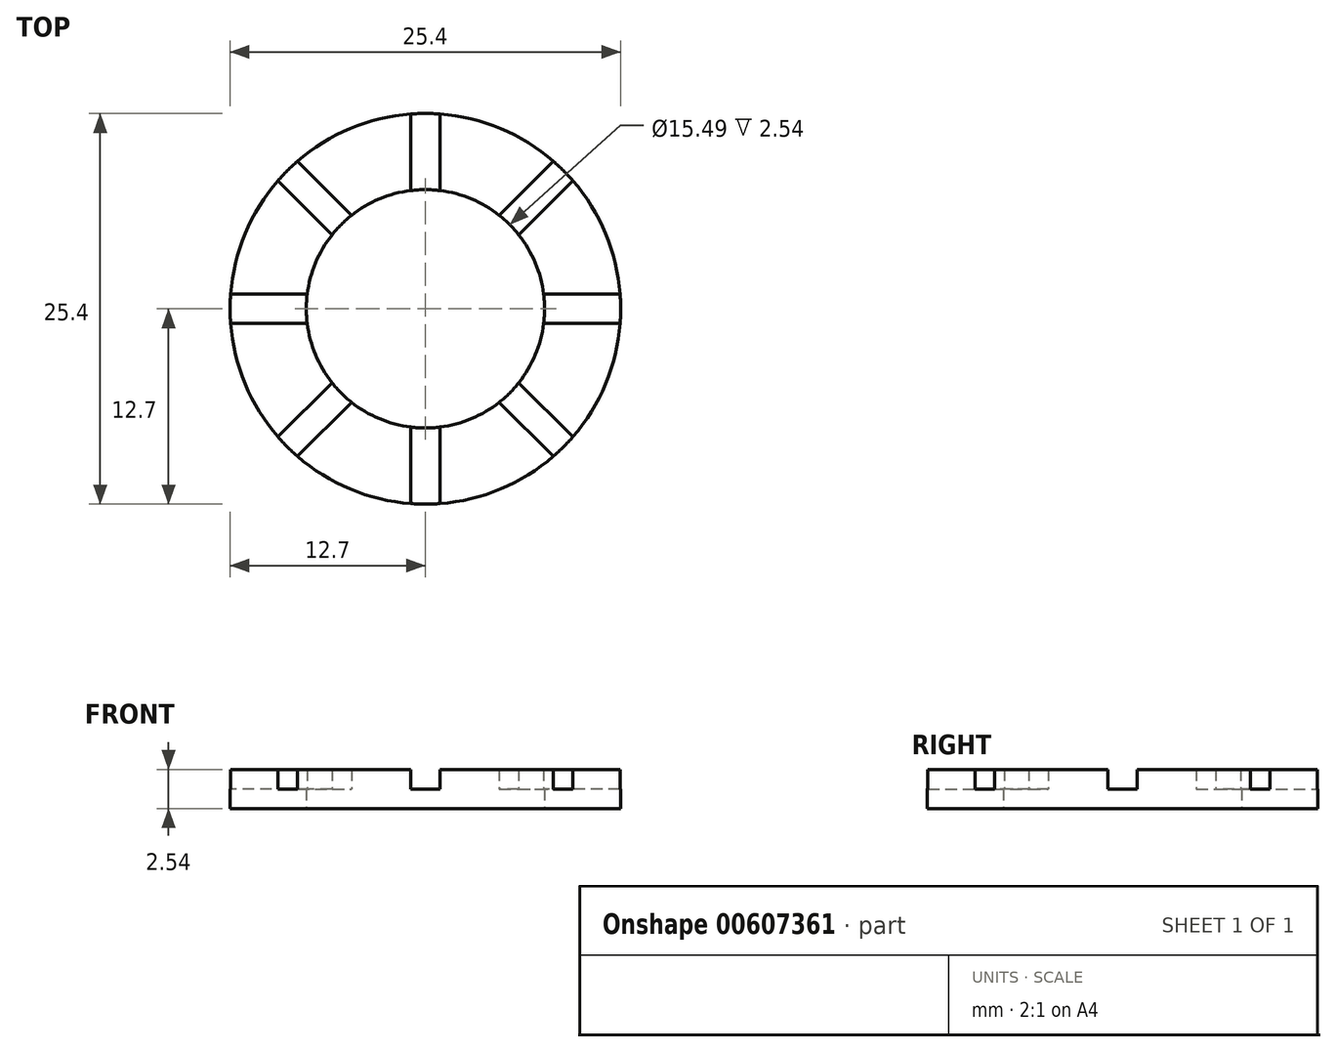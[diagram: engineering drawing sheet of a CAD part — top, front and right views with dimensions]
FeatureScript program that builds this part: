
annotation { "Feature Type Name" : "Feature", "Feature Type Description" : "" }
export const myFeature = defineFeature(function(context is Context, id is Id, definition is map)
    precondition{}
    {
        {
            var Q0;
            Q0=qCreatedBy(makeId("Top.planeOp"),FACE);
            var sketch = newSketch(context, id + "F0", { "sketchPlane" : qUnion([Q0])});
            skCircle(sketch, "E0", {"center": v(0, 0) * mm, "radius": 7.75 * mm});
            skCircle(sketch, "E1", {"center": v(0, 0) * mm, "radius": 12.7 * mm});
            skSolve(sketch);
        }
        {
            var Q0;
            Q0=makeQuery(id+"F0.imprint","IMPRINT",FACE,{"disambiguationData":[TD([[makeQuery(id+"F0.imprint","IMPRINT",EDGE,{"derivedFrom":sQuery(id+"F0.wireOp",EDGE,"E0")}),-1.0]])]});
            extrude(context, id + "F1", {"entities" : qUnion([Q0]), "depth" : 2.54 * mm, "offsetDistance" : 25.4 * mm});
        }
        {
            var Q0;
            Q0=makeQuery(id+"F1.opExtrude","CAP_FACE",FACE,{"disambiguationData":[OSD([sQuery(id+"F0.wireOp",EDGE,"E0"),sQuery(id+"F0.wireOp",EDGE,"E1")])],"isStart":false});
            var sketch = newSketch(context, id + "F2", { "sketchPlane" : qUnion([Q0])});
            skPoint(sketch, "E2", {"position": v(0, 0) * mm});
            skLineSegment(sketch, "E3", {"start": v(0, 0) * mm, "end": v(6.35, 6.35) * mm});
            skLineSegment(sketch, "E4", {"start": v(0, 0) * mm, "end": v(-6.35, 6.35) * mm});
            skLineSegment(sketch, "E5", {"start": v(0, 0) * mm, "end": v(6.35, -6.35) * mm});
            skLineSegment(sketch, "E6", {"start": v(0, 0) * mm, "end": v(-6.35, -6.35) * mm});
            skLineSegment(sketch, "E7", {"start": v(0, 0) * mm, "end": v(-9.7, -9.7) * mm});
            skLineSegment(sketch, "E8", {"start": v(0, 0) * mm, "end": v(9.7, -9.7) * mm});
            skLineSegment(sketch, "E9", {"start": v(0, 0) * mm, "end": v(-9.7, 9.7) * mm});
            skLineSegment(sketch, "E10", {"start": v(0, 0) * mm, "end": v(9.7, 9.7) * mm});
            skLineSegment(sketch, "E11", {"start": v(0, 0) * mm, "end": v(1.27, 0) * mm});
            skLineSegment(sketch, "E12", {"start": v(0, 0) * mm, "end": v(0, 1.27) * mm});
            skLineSegment(sketch, "E13", {"start": v(9.7, 9.7) * mm, "end": v(9.7, 8.43) * mm});
            skLineSegment(sketch, "E14", {"start": v(9.7, 9.7) * mm, "end": v(8.43, 9.7) * mm});
            skLineSegment(sketch, "E15", {"start": v(0, 1.27) * mm, "end": v(8.43, 9.7) * mm});
            skLineSegment(sketch, "E16", {"start": v(1.27, 0) * mm, "end": v(9.7, 8.43) * mm});
            skLineSegment(sketch, "E17", {"start": v(0, 0) * mm, "end": v(0, -1.27) * mm});
            skLineSegment(sketch, "E18", {"start": v(9.7, -9.7) * mm, "end": v(9.7, -8.43) * mm});
            skLineSegment(sketch, "E19", {"start": v(9.7, -9.7) * mm, "end": v(8.43, -9.7) * mm});
            skLineSegment(sketch, "E20", {"start": v(1.27, 0) * mm, "end": v(9.7, -8.43) * mm});
            skLineSegment(sketch, "E21", {"start": v(0, -1.27) * mm, "end": v(8.43, -9.7) * mm});
            skLineSegment(sketch, "E22", {"start": v(0, 0) * mm, "end": v(-1.27, 0) * mm});
            skLineSegment(sketch, "E23", {"start": v(-9.7, -9.7) * mm, "end": v(-8.43, -9.7) * mm});
            skLineSegment(sketch, "E24", {"start": v(-9.7, -9.7) * mm, "end": v(-9.7, -8.43) * mm});
            skLineSegment(sketch, "E25", {"start": v(-8.43, -9.7) * mm, "end": v(0, -1.27) * mm});
            skLineSegment(sketch, "E26", {"start": v(-9.7, -8.43) * mm, "end": v(-1.27, 0) * mm});
            skLineSegment(sketch, "E27", {"start": v(-9.7, 9.7) * mm, "end": v(-9.7, 8.43) * mm});
            skLineSegment(sketch, "E28", {"start": v(-9.7, 9.7) * mm, "end": v(-8.43, 9.7) * mm});
            skLineSegment(sketch, "E29", {"start": v(-8.43, 9.7) * mm, "end": v(0, 1.27) * mm});
            skLineSegment(sketch, "E30", {"start": v(-1.27, 0) * mm, "end": v(-9.7, 8.43) * mm});
            skSolve(sketch);
        }
        {
            var Q0;
            Q0 = qSketchRegion(id + "F2", true);
            extrude(context, id + "F3", {"entities" : qUnion([Q0]), "operationType" : NewBodyOperationType.REMOVE, "oppositeDirection" : true, "depth" : 1.27 * mm, "offsetDistance" : 25.4 * mm});
        }
        {
            var Q0;
            {var subQ0=sQuery(id+"F0.wireOp",EDGE,"E0");var subQ1=sQuery(id+"F0.wireOp",EDGE,"E1");Q0=makeQuery(id+"F3.boolean.opBoolean","SPLIT",FACE,{"disambiguationData":[TD([makeQuery(id+"F3.opExtrude","SWEPT_FACE",FACE,{"disambiguationData":[OSD([sQuery(id+"F2.wireOp",EDGE,"E15")])]})])],"derivedFrom":makeQuery(id+"F1.opExtrude","CAP_FACE",FACE,{"disambiguationData":[OSD([subQ0,subQ1])],"isStart":false})});}
            var sketch = newSketch(context, id + "F4", { "sketchPlane" : qUnion([Q0])});
            skLineSegment(sketch, "E31.bottom", {"start": v(0.95, -12.7) * mm, "end": v(-0.95, -12.7) * mm});
            skLineSegment(sketch, "E31.top", {"start": v(0.95, 12.7) * mm, "end": v(-0.95, 12.7) * mm});
            skLineSegment(sketch, "E31.left", {"start": v(0.95, -12.7) * mm, "end": v(0.95, 12.7) * mm});
            skLineSegment(sketch, "E31.right", {"start": v(-0.95, -12.7) * mm, "end": v(-0.95, 12.7) * mm});
            skPoint(sketch, "E31.middle", {"position": v(0, 0) * mm});
            skLineSegment(sketch, "E32.bottom", {"start": v(12.7, -0.95) * mm, "end": v(-12.7, -0.95) * mm});
            skLineSegment(sketch, "E32.top", {"start": v(12.7, 0.95) * mm, "end": v(-12.7, 0.95) * mm});
            skLineSegment(sketch, "E32.left", {"start": v(12.7, -0.95) * mm, "end": v(12.7, 0.95) * mm});
            skLineSegment(sketch, "E32.right", {"start": v(-12.7, -0.95) * mm, "end": v(-12.7, 0.95) * mm});
            skSolve(sketch);
        }
        {
            var Q0;
            Q0 = qSketchRegion(id + "F4", true);
            extrude(context, id + "F5", {"entities" : qUnion([Q0]), "operationType" : NewBodyOperationType.REMOVE, "oppositeDirection" : true, "depth" : 1.27 * mm, "offsetDistance" : 25.4 * mm});
        }
    });
